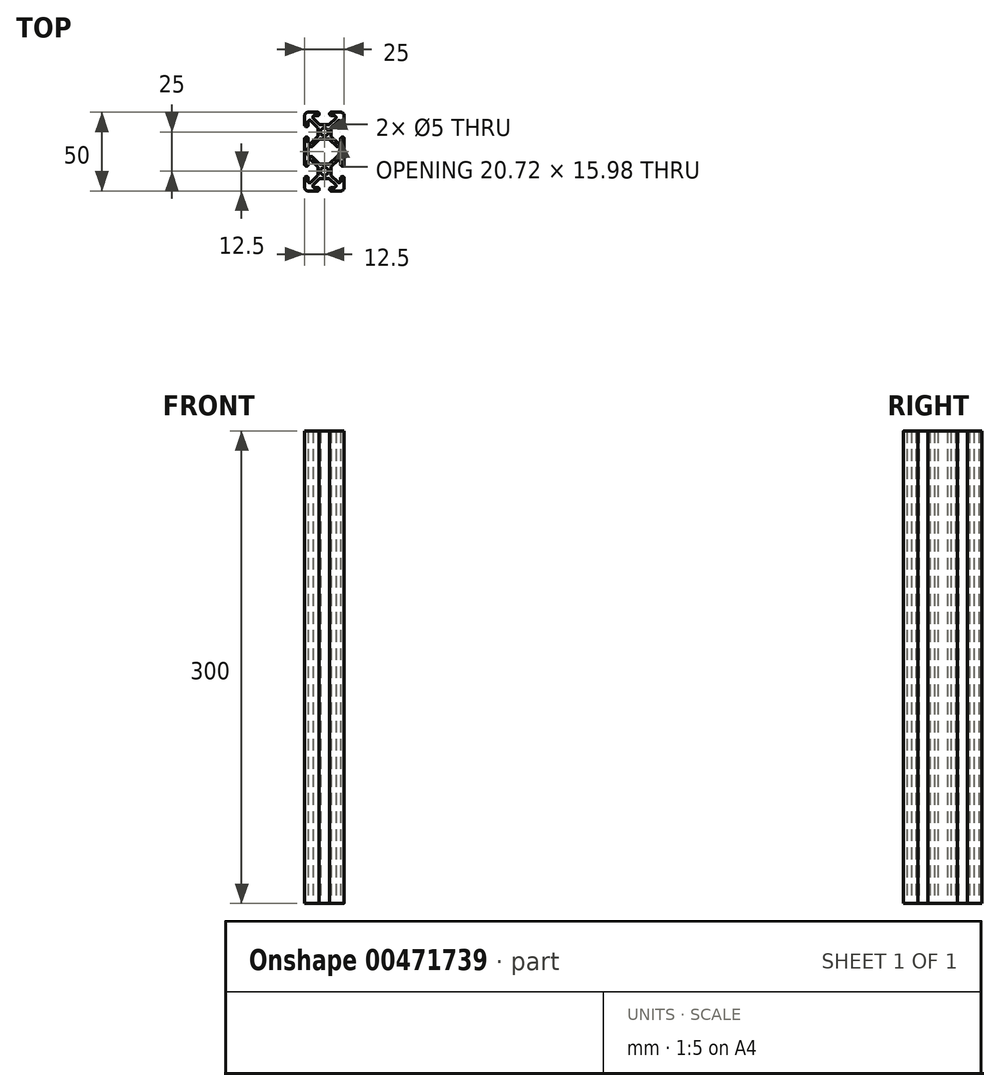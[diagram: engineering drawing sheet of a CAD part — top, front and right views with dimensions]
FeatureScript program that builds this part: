
annotation { "Feature Type Name" : "Feature", "Feature Type Description" : "" }
export const myFeature = defineFeature(function(context is Context, id is Id, definition is map)
    precondition{}
    {
        {
            var Q0;
            Q0=qCreatedBy(makeId("Top.planeOp"),FACE);
            var sketch = newSketch(context, id + "F0", { "sketchPlane" : qUnion([Q0])});
            skCircle(sketch, "E0", {"center": v(0, 0) * mm, "radius": 2.5 * mm});
            skLineSegment(sketch, "E1", {"start": v(0, 0) * mm, "end": v(0, 4.5) * mm, "construction": true});
            skLineSegment(sketch, "E2", {"start": v(0, 0) * mm, "end": v(-4.05, 0) * mm, "construction": true});
            skLineSegment(sketch, "E3", {"start": v(0, 0) * mm, "end": v(-12.5, 12.5) * mm, "construction": true});
            skLineSegment(sketch, "E4", {"start": v(-12.5, 10.36) * mm, "end": v(-12.5, 4.32) * mm});
            skLineSegment(sketch, "E5", {"start": v(-10.36, 12.5) * mm, "end": v(-4.32, 12.5) * mm});
            skLineSegment(sketch, "E6", {"start": v(-4.32, 10.36) * mm, "end": v(-6.26, 10.36) * mm});
            skLineSegment(sketch, "E7", {"start": v(-10.36, 6.26) * mm, "end": v(-10.36, 4.32) * mm});
            skArc(sketch, "E8", {"start": v(-4.32, 12.5) * mm, "mid": v(-3.25, 11.43) * mm, "end": v(-4.32, 10.36) * mm});
            skArc(sketch, "E9", {"start": v(-10.36, 4.32) * mm, "mid": v(-11.43, 3.25) * mm, "end": v(-12.5, 4.32) * mm});
            skLineSegment(sketch, "E10", {"start": v(0, 4.5) * mm, "end": v(-2.55, 4.5) * mm});
            skLineSegment(sketch, "E11", {"start": v(-4.05, 2.1) * mm, "end": v(-4.05, 0) * mm});
            skLineSegment(sketch, "E12", {"start": v(-8.53, 7.02) * mm, "end": v(-4.36, 2.85) * mm});
            skLineSegment(sketch, "E13", {"start": v(-7.02, 8.53) * mm, "end": v(-3.31, 4.82) * mm});
            skLineSegment(sketch, "E14.0.MirrorCS", {"start": v(10.36, 6.26) * mm, "end": v(10.36, 4.32) * mm});
            skLineSegment(sketch, "E14.1.MirrorCS", {"start": v(7.02, 8.53) * mm, "end": v(3.31, 4.82) * mm});
            skArc(sketch, "E14.2.MirrorCS", {"start": v(4.32, 12.5) * mm, "mid": v(3.25, 11.43) * mm, "end": v(4.32, 10.36) * mm});
            skArc(sketch, "E14.3.MirrorCS", {"start": v(10.36, 4.32) * mm, "mid": v(11.43, 3.25) * mm, "end": v(12.5, 4.32) * mm});
            skLineSegment(sketch, "E14.4.MirrorCS", {"start": v(10.36, 12.5) * mm, "end": v(4.32, 12.5) * mm});
            skLineSegment(sketch, "E14.5.MirrorCS", {"start": v(4.32, 10.36) * mm, "end": v(6.26, 10.36) * mm});
            skLineSegment(sketch, "E14.6.MirrorCS", {"start": v(12.5, 10.36) * mm, "end": v(12.5, 4.32) * mm});
            skLineSegment(sketch, "E14.7.MirrorCS", {"start": v(8.53, 7.02) * mm, "end": v(4.36, 2.85) * mm});
            skLineSegment(sketch, "E15.0.MirrorCS", {"start": v(0, 4.5) * mm, "end": v(2.55, 4.5) * mm});
            skLineSegment(sketch, "E16.0.MirrorCS", {"start": v(4.05, 2.1) * mm, "end": v(4.05, 0) * mm});
            skLineSegment(sketch, "E17.1.MirrorCS", {"start": v(12.5, -12.5) * mm, "end": v(12.5, -4.32) * mm});
            skLineSegment(sketch, "E17.5.MirrorCS", {"start": v(10.36, -6.26) * mm, "end": v(10.36, -4.32) * mm});
            skLineSegment(sketch, "E17.6.MirrorCS", {"start": v(8.53, -7.02) * mm, "end": v(4.36, -2.85) * mm});
            skArc(sketch, "E17.10.MirrorCS", {"start": v(10.36, -4.32) * mm, "mid": v(11.43, -3.25) * mm, "end": v(12.5, -4.32) * mm});
            skLineSegment(sketch, "E17.11.MirrorCS", {"start": v(-12.5, -12.5) * mm, "end": v(-12.5, -4.32) * mm});
            skLineSegment(sketch, "E17.14.MirrorCS", {"start": v(-8.53, -7.02) * mm, "end": v(-4.36, -2.85) * mm});
            skArc(sketch, "E17.15.MirrorCS", {"start": v(-10.36, -4.32) * mm, "mid": v(-11.43, -3.25) * mm, "end": v(-12.5, -4.32) * mm});
            skLineSegment(sketch, "E17.16.MirrorCS", {"start": v(-10.36, -6.26) * mm, "end": v(-10.36, -4.32) * mm});
            skLineSegment(sketch, "E18.0.MirrorCS", {"start": v(4.05, -2.1) * mm, "end": v(4.05, 0) * mm});
            skLineSegment(sketch, "E19.0.MirrorCS", {"start": v(-4.05, -2.1) * mm, "end": v(-4.05, 0) * mm});
            skPoint(sketch, "E20.visualSharp", {"position": v(-12.5, 12.5) * mm});
            skArc(sketch, "E20.filletArc", {"start": v(-10.36, 12.5) * mm, "mid": v(-11.87, 11.87) * mm, "end": v(-12.5, 10.36) * mm});
            skPoint(sketch, "E21.visualSharp", {"position": v(12.5, 12.5) * mm});
            skArc(sketch, "E21.filletArc", {"start": v(12.5, 10.36) * mm, "mid": v(11.87, 11.87) * mm, "end": v(10.36, 12.5) * mm});
            skPoint(sketch, "E22.visualSharp", {"position": v(-12.5, -12.5) * mm});
            skPoint(sketch, "E23.visualSharp", {"position": v(4.05, 4.5) * mm});
            skPoint(sketch, "E24.visualSharp", {"position": v(-10.36, 8.85) * mm});
            skArc(sketch, "E24.filletArc", {"start": v(-8.53, 7.02) * mm, "mid": v(-9.7, 7.25) * mm, "end": v(-10.36, 6.26) * mm});
            skPoint(sketch, "E25.visualSharp", {"position": v(-8.85, 10.36) * mm});
            skArc(sketch, "E25.filletArc", {"start": v(-6.26, 10.36) * mm, "mid": v(-7.25, 9.7) * mm, "end": v(-7.02, 8.53) * mm});
            skPoint(sketch, "E26.visualSharp", {"position": v(8.85, 10.36) * mm});
            skArc(sketch, "E26.filletArc", {"start": v(7.02, 8.53) * mm, "mid": v(7.25, 9.7) * mm, "end": v(6.26, 10.36) * mm});
            skArc(sketch, "E27.filletArc", {"start": v(10.36, 6.26) * mm, "mid": v(9.7, 7.25) * mm, "end": v(8.53, 7.02) * mm});
            skArc(sketch, "E28.filletArc", {"start": v(8.53, -7.02) * mm, "mid": v(9.7, -7.25) * mm, "end": v(10.36, -6.26) * mm});
            skArc(sketch, "E29.filletArc", {"start": v(-10.36, -6.26) * mm, "mid": v(-9.7, -7.25) * mm, "end": v(-8.53, -7.02) * mm});
            skPoint(sketch, "E30.orphan", {"position": v(-4.05, 4.5) * mm});
            skPoint(sketch, "E31.visualSharp", {"position": v(-3, 4.5) * mm});
            skArc(sketch, "E31.filletArc", {"start": v(-3.31, 4.82) * mm, "mid": v(-2.96, 4.6) * mm, "end": v(-2.55, 4.5) * mm});
            skPoint(sketch, "E32.visualSharp", {"position": v(3, 4.5) * mm});
            skArc(sketch, "E32.filletArc", {"start": v(2.55, 4.5) * mm, "mid": v(2.96, 4.6) * mm, "end": v(3.31, 4.82) * mm});
            skPoint(sketch, "E33.visualSharp", {"position": v(-4.05, 2.54) * mm});
            skArc(sketch, "E33.filletArc", {"start": v(-4.05, 2.1) * mm, "mid": v(-4.13, 2.5) * mm, "end": v(-4.36, 2.85) * mm});
            skPoint(sketch, "E34.visualSharp", {"position": v(-4.05, -2.54) * mm});
            skArc(sketch, "E34.filletArc", {"start": v(-4.36, -2.85) * mm, "mid": v(-4.13, -2.5) * mm, "end": v(-4.05, -2.1) * mm});
            skPoint(sketch, "E35.visualSharp", {"position": v(4.05, -2.54) * mm});
            skArc(sketch, "E35.filletArc", {"start": v(4.05, -2.1) * mm, "mid": v(4.13, -2.5) * mm, "end": v(4.36, -2.85) * mm});
            skPoint(sketch, "E36.visualSharp", {"position": v(4.05, 2.54) * mm});
            skArc(sketch, "E36.filletArc", {"start": v(4.36, 2.85) * mm, "mid": v(4.13, 2.5) * mm, "end": v(4.05, 2.1) * mm});
            skCircle(sketch, "E37", {"center": v(0, -25) * mm, "radius": 2.5 * mm});
            skLineSegment(sketch, "E38", {"start": v(0, 0) * mm, "end": v(0, -25) * mm, "construction": true});
            skLineSegment(sketch, "E39", {"start": v(0, -12.5) * mm, "end": v(3.65, -12.5) * mm, "construction": true});
            skArc(sketch, "E40.0.MirrorCS", {"start": v(2.55, -29.51) * mm, "mid": v(2.96, -29.6) * mm, "end": v(3.31, -29.82) * mm});
            skArc(sketch, "E40.1.MirrorCS", {"start": v(4.36, -27.85) * mm, "mid": v(4.13, -27.5) * mm, "end": v(4.05, -27.1) * mm});
            skArc(sketch, "E40.2.MirrorCS", {"start": v(-4.05, -27.1) * mm, "mid": v(-4.13, -27.5) * mm, "end": v(-4.36, -27.85) * mm});
            skArc(sketch, "E40.3.MirrorCS", {"start": v(-4.36, -22.15) * mm, "mid": v(-4.13, -22.5) * mm, "end": v(-4.05, -22.9) * mm});
            skArc(sketch, "E40.4.MirrorCS", {"start": v(-3.31, -29.82) * mm, "mid": v(-2.96, -29.6) * mm, "end": v(-2.55, -29.51) * mm});
            skArc(sketch, "E40.5.MirrorCS", {"start": v(4.05, -22.9) * mm, "mid": v(4.13, -22.5) * mm, "end": v(4.36, -22.15) * mm});
            skPoint(sketch, "E40.6.MirrorP", {"position": v(-4.05, -27.54) * mm});
            skPoint(sketch, "E40.7.MirrorP", {"position": v(-10.36, -33.85) * mm});
            skPoint(sketch, "E40.8.MirrorP", {"position": v(4.05, -27.54) * mm});
            skLineSegment(sketch, "E40.10.MirrorCS", {"start": v(0, -25) * mm, "end": v(0, -29.51) * mm, "construction": true});
            skLineSegment(sketch, "E40.11.MirrorCS", {"start": v(-12.5, -35.36) * mm, "end": v(-12.5, -29.32) * mm});
            skLineSegment(sketch, "E40.12.MirrorCS", {"start": v(0, -25) * mm, "end": v(-12.5, -37.5) * mm, "construction": true});
            skLineSegment(sketch, "E40.13.MirrorCS", {"start": v(-4.32, -35.36) * mm, "end": v(-6.26, -35.36) * mm});
            skLineSegment(sketch, "E40.14.MirrorCS", {"start": v(-10.36, -31.26) * mm, "end": v(-10.36, -29.32) * mm});
            skLineSegment(sketch, "E40.15.MirrorCS", {"start": v(0, -29.51) * mm, "end": v(-2.55, -29.51) * mm});
            skPoint(sketch, "E40.16.MirrorP", {"position": v(10.36, -33.85) * mm});
            skLineSegment(sketch, "E40.17.MirrorCS", {"start": v(-4.05, -22.9) * mm, "end": v(-4.05, -25) * mm});
            skLineSegment(sketch, "E40.18.MirrorCS", {"start": v(-8.53, -32.02) * mm, "end": v(-4.36, -27.85) * mm});
            skArc(sketch, "E40.19.MirrorCS", {"start": v(10.36, -29.32) * mm, "mid": v(11.43, -28.25) * mm, "end": v(12.5, -29.32) * mm});
            skArc(sketch, "E40.20.MirrorCS", {"start": v(8.53, -17.98) * mm, "mid": v(9.7, -17.75) * mm, "end": v(10.36, -18.74) * mm});
            skLineSegment(sketch, "E40.21.MirrorCS", {"start": v(-4.05, -27.1) * mm, "end": v(-4.05, -25) * mm});
            skLineSegment(sketch, "E40.22.MirrorCS", {"start": v(12.5, -12.5) * mm, "end": v(12.5, -20.68) * mm});
            skLineSegment(sketch, "E40.23.MirrorCS", {"start": v(8.53, -32.02) * mm, "end": v(4.36, -27.85) * mm});
            skPoint(sketch, "E40.24.MirrorP", {"position": v(-8.85, -35.36) * mm});
            skArc(sketch, "E40.25.MirrorCS", {"start": v(-6.26, -35.36) * mm, "mid": v(-7.25, -34.7) * mm, "end": v(-7.02, -33.53) * mm});
            skArc(sketch, "E40.26.MirrorCS", {"start": v(10.36, -20.68) * mm, "mid": v(11.43, -21.75) * mm, "end": v(12.5, -20.68) * mm});
            skPoint(sketch, "E40.28.MirrorP", {"position": v(-3, -29.51) * mm});
            skLineSegment(sketch, "E40.29.MirrorCS", {"start": v(10.36, -31.26) * mm, "end": v(10.36, -29.32) * mm});
            skLineSegment(sketch, "E40.30.MirrorCS", {"start": v(7.02, -33.53) * mm, "end": v(3.31, -29.82) * mm});
            skPoint(sketch, "E40.31.MirrorP", {"position": v(12.5, -37.5) * mm});
            skLineSegment(sketch, "E40.32.MirrorCS", {"start": v(-10.36, -18.74) * mm, "end": v(-10.36, -20.68) * mm});
            skArc(sketch, "E40.33.MirrorCS", {"start": v(12.5, -35.36) * mm, "mid": v(11.87, -36.87) * mm, "end": v(10.36, -37.5) * mm});
            skArc(sketch, "E40.35.MirrorCS", {"start": v(-10.36, -37.5) * mm, "mid": v(-11.87, -36.87) * mm, "end": v(-12.5, -35.36) * mm});
            skPoint(sketch, "E40.37.MirrorP", {"position": v(-4.05, -22.46) * mm});
            skPoint(sketch, "E40.38.MirrorP", {"position": v(8.85, -35.36) * mm});
            skArc(sketch, "E40.39.MirrorCS", {"start": v(10.36, -31.26) * mm, "mid": v(9.7, -32.25) * mm, "end": v(8.53, -32.02) * mm});
            skLineSegment(sketch, "E40.40.MirrorCS", {"start": v(-8.53, -17.98) * mm, "end": v(-4.36, -22.15) * mm});
            skLineSegment(sketch, "E40.42.MirrorCS", {"start": v(8.53, -17.98) * mm, "end": v(4.36, -22.15) * mm});
            skLineSegment(sketch, "E40.43.MirrorCS", {"start": v(4.05, -22.9) * mm, "end": v(4.05, -25) * mm});
            skArc(sketch, "E40.44.MirrorCS", {"start": v(4.32, -37.5) * mm, "mid": v(3.25, -36.43) * mm, "end": v(4.32, -35.36) * mm});
            skArc(sketch, "E40.45.MirrorCS", {"start": v(-10.36, -18.74) * mm, "mid": v(-9.7, -17.75) * mm, "end": v(-8.53, -17.98) * mm});
            skLineSegment(sketch, "E40.46.MirrorCS", {"start": v(10.36, -18.74) * mm, "end": v(10.36, -20.68) * mm});
            skPoint(sketch, "E40.47.MirrorP", {"position": v(3, -29.51) * mm});
            skPoint(sketch, "E40.48.MirrorP", {"position": v(-4.05, -29.51) * mm});
            skLineSegment(sketch, "E40.49.MirrorCS", {"start": v(0, -29.51) * mm, "end": v(2.55, -29.51) * mm});
            skArc(sketch, "E40.51.MirrorCS", {"start": v(7.02, -33.53) * mm, "mid": v(7.25, -34.7) * mm, "end": v(6.26, -35.36) * mm});
            skPoint(sketch, "E40.52.MirrorP", {"position": v(-12.5, -37.5) * mm});
            skArc(sketch, "E40.53.MirrorCS", {"start": v(-10.36, -20.68) * mm, "mid": v(-11.43, -21.75) * mm, "end": v(-12.5, -20.68) * mm});
            skLineSegment(sketch, "E40.54.MirrorCS", {"start": v(0, -25) * mm, "end": v(-4.05, -25) * mm, "construction": true});
            skLineSegment(sketch, "E40.55.MirrorCS", {"start": v(-10.36, -37.5) * mm, "end": v(-4.32, -37.5) * mm});
            skArc(sketch, "E40.56.MirrorCS", {"start": v(-4.32, -37.5) * mm, "mid": v(-3.25, -36.43) * mm, "end": v(-4.32, -35.36) * mm});
            skArc(sketch, "E40.57.MirrorCS", {"start": v(-10.36, -29.32) * mm, "mid": v(-11.43, -28.25) * mm, "end": v(-12.5, -29.32) * mm});
            skPoint(sketch, "E40.58.MirrorP", {"position": v(4.05, -29.51) * mm});
            skLineSegment(sketch, "E40.59.MirrorCS", {"start": v(-7.02, -33.53) * mm, "end": v(-3.31, -29.82) * mm});
            skLineSegment(sketch, "E40.60.MirrorCS", {"start": v(10.36, -37.5) * mm, "end": v(4.32, -37.5) * mm});
            skLineSegment(sketch, "E40.61.MirrorCS", {"start": v(4.05, -27.1) * mm, "end": v(4.05, -25) * mm});
            skPoint(sketch, "E40.62.MirrorP", {"position": v(4.05, -22.46) * mm});
            skArc(sketch, "E40.63.MirrorCS", {"start": v(-8.53, -32.02) * mm, "mid": v(-9.7, -32.25) * mm, "end": v(-10.36, -31.26) * mm});
            skLineSegment(sketch, "E40.64.MirrorCS", {"start": v(12.5, -35.36) * mm, "end": v(12.5, -29.32) * mm});
            skLineSegment(sketch, "E40.65.MirrorCS", {"start": v(-12.5, -12.5) * mm, "end": v(-12.5, -20.68) * mm});
            skLineSegment(sketch, "E40.67.MirrorCS", {"start": v(4.32, -35.36) * mm, "end": v(6.26, -35.36) * mm});
            skLineSegment(sketch, "E41.0.MirrorCS", {"start": v(0, -4.5) * mm, "end": v(-2.55, -4.5) * mm});
            skPoint(sketch, "E42.visualSharp", {"position": v(-2.55, -4.5) * mm});
            skLineSegment(sketch, "E43", {"start": v(-10.36, -10.54) * mm, "end": v(-10.36, -12.5) * mm});
            skLineSegment(sketch, "E44", {"start": v(-9.3, -9.47) * mm, "end": v(-8.4, -9.47) * mm});
            skLineSegment(sketch, "E45", {"start": v(-3.31, -4.82) * mm, "end": v(-7.65, -9.16) * mm});
            skPoint(sketch, "E46.visualSharp", {"position": v(-3, -4.5) * mm});
            skArc(sketch, "E46.filletArc", {"start": v(-2.55, -4.5) * mm, "mid": v(-2.96, -4.6) * mm, "end": v(-3.31, -4.82) * mm});
            skPoint(sketch, "E47.visualSharp", {"position": v(-7.96, -9.47) * mm});
            skArc(sketch, "E47.filletArc", {"start": v(-8.4, -9.47) * mm, "mid": v(-8, -9.4) * mm, "end": v(-7.65, -9.16) * mm});
            skPoint(sketch, "E48.visualSharp", {"position": v(-10.36, -9.47) * mm});
            skArc(sketch, "E48.filletArc", {"start": v(-9.3, -9.47) * mm, "mid": v(-10.05, -9.79) * mm, "end": v(-10.36, -10.54) * mm});
            skLineSegment(sketch, "E49.0.MirrorCS", {"start": v(0, -4.5) * mm, "end": v(2.55, -4.5) * mm});
            skArc(sketch, "E50.0.MirrorCS", {"start": v(2.55, -4.5) * mm, "mid": v(2.96, -4.6) * mm, "end": v(3.31, -4.82) * mm});
            skLineSegment(sketch, "E51.0.MirrorCS", {"start": v(3.31, -4.82) * mm, "end": v(7.65, -9.16) * mm});
            skPoint(sketch, "E52.0.MirrorP", {"position": v(7.96, -9.47) * mm});
            skArc(sketch, "E53.0.MirrorCS", {"start": v(8.4, -9.47) * mm, "mid": v(8, -9.4) * mm, "end": v(7.65, -9.16) * mm});
            skLineSegment(sketch, "E54.0.MirrorCS", {"start": v(9.3, -9.47) * mm, "end": v(8.4, -9.47) * mm});
            skArc(sketch, "E55.0.MirrorCS", {"start": v(9.3, -9.47) * mm, "mid": v(10.05, -9.79) * mm, "end": v(10.36, -10.54) * mm});
            skLineSegment(sketch, "E56.0.MirrorCS", {"start": v(10.36, -10.54) * mm, "end": v(10.36, -12.5) * mm});
            skLineSegment(sketch, "E57.0.MirrorCS", {"start": v(10.36, -14.46) * mm, "end": v(10.36, -12.5) * mm});
            skArc(sketch, "E58.0.MirrorCS", {"start": v(9.3, -15.53) * mm, "mid": v(10.05, -15.21) * mm, "end": v(10.36, -14.46) * mm});
            skLineSegment(sketch, "E59.0.MirrorCS", {"start": v(9.3, -15.53) * mm, "end": v(8.4, -15.53) * mm});
            skArc(sketch, "E60.0.MirrorCS", {"start": v(8.4, -15.53) * mm, "mid": v(8, -15.6) * mm, "end": v(7.65, -15.84) * mm});
            skLineSegment(sketch, "E61.0.MirrorCS", {"start": v(3.31, -20.18) * mm, "end": v(7.65, -15.84) * mm});
            skArc(sketch, "E62.0.MirrorCS", {"start": v(2.55, -20.5) * mm, "mid": v(2.96, -20.4) * mm, "end": v(3.31, -20.18) * mm});
            skLineSegment(sketch, "E63.0.MirrorCS", {"start": v(0, -20.5) * mm, "end": v(2.55, -20.5) * mm});
            skLineSegment(sketch, "E64.0.MirrorCS", {"start": v(0, -20.5) * mm, "end": v(-2.55, -20.5) * mm});
            skArc(sketch, "E65.0.MirrorCS", {"start": v(-2.55, -20.5) * mm, "mid": v(-2.96, -20.4) * mm, "end": v(-3.31, -20.18) * mm});
            skLineSegment(sketch, "E66.0.MirrorCS", {"start": v(-3.31, -20.18) * mm, "end": v(-7.65, -15.84) * mm});
            skArc(sketch, "E67.0.MirrorCS", {"start": v(-8.4, -15.53) * mm, "mid": v(-8, -15.6) * mm, "end": v(-7.65, -15.84) * mm});
            skLineSegment(sketch, "E68.0.MirrorCS", {"start": v(-9.3, -15.53) * mm, "end": v(-8.4, -15.53) * mm});
            skArc(sketch, "E69.0.MirrorCS", {"start": v(-9.3, -15.53) * mm, "mid": v(-10.05, -15.21) * mm, "end": v(-10.36, -14.46) * mm});
            skLineSegment(sketch, "E70.0.MirrorCS", {"start": v(-10.36, -14.46) * mm, "end": v(-10.36, -12.5) * mm});
            skSolve(sketch);
        }
        {
            var Q0;
            Q0=makeQuery(id+"F0.imprint","IMPRINT",FACE,{"disambiguationData":[TD([[makeQuery(id+"F0.imprint","IMPRINT",EDGE,{"derivedFrom":sQuery(id+"F0.wireOp",EDGE,"E0")}),-1.0]])]});
            extrude(context, id + "F1", {"entities" : qUnion([Q0]), "depth" : 300 * mm});
        }
    });
